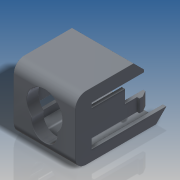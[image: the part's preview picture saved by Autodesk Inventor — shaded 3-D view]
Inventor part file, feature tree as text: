
AUTODESK INVENTOR PART (.ipt)
format: ipt  version: 2016 SP2 (Build 200236200, 236)  size: 454,656 bytes
history: native  units: in
note: dims shown in document units (in); Inventor stores cm internally (conversion verified against a paired STEP export)
features: extrude x6, sketch x4, fillet x1, projected_geometry x1
ambient origin geometry x8: Origin, YZ Plane, XZ Plane, XY Plane, X Axis, Y Axis, Z Axis, Center Point
bodies: Solid1 (feature_tree)
feature tree (12):
  sketch  "Sketch2"  dims[d0=0.8504in d1=0.1417in]
  extrude  "Extrusion1"  Depth=0.1417in
  extrude  "Extrusion2"  Depth=0.2205in
  extrude  "Extrusion5"  Depth=0.1417in
  extrude  "Extrusion6"  Depth=0.3937in
  extrude  "Extrusion8"  Depth=0.3937in
  extrude  "Extrusion9"  Depth=0.3937in
  fillet  "Fillet1"  Radius=0.9134in
  sketch  "Sketch3"  dims[d2=1.2126in d3=0.2205in]
  projected_geometry  "Projected Loop1"
  sketch  "Sketch5"  dims[d4=45.0deg d5=0.1417in]
  sketch  "Sketch6"  dims[d6=0.1732in d7=0.1732in d8=0.1732in d9=0.0315in d10=0.9134in d11=0.063in d12=0.6614in d13=0.8189in d14=0.0567in d15=0.0472in d16=0.063in d21=0.5669in d22=0.8189in d23=0.0in d24=0.7244in d25=0.0in d30=0.315in d31=0.0in d32=0.126in d33=0.0315in d34=0.0472in d35=0.0315in d36=0.315in d37=0.0in d50=0.0039in d51=0.4724in d52=0.3386in d53=0.2047in d54=0.1181in d55=0.5669in d56=0.4063in d57=0.3937in d58=0.0in d59=0.0945in d60=0.0in]
